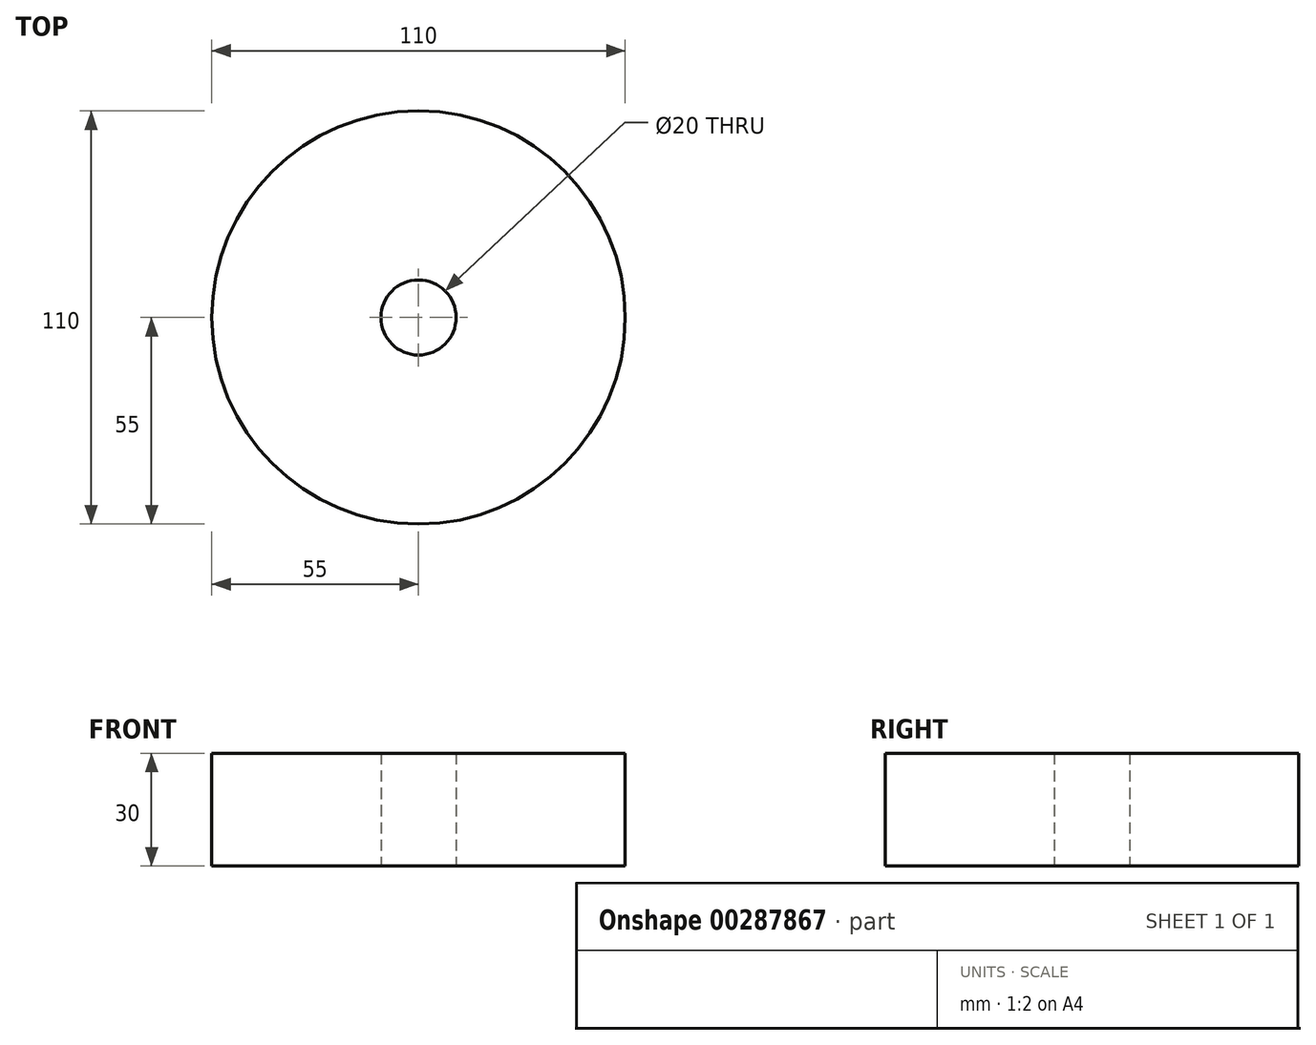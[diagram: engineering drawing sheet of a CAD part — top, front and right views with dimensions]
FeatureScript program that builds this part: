
annotation { "Feature Type Name" : "Feature", "Feature Type Description" : "" }
export const myFeature = defineFeature(function(context is Context, id is Id, definition is map)
    precondition{}
    {
        {
            var Q0;
            Q0=qCreatedBy(makeId("Top.planeOp"),FACE);
            var sketch = newSketch(context, id + "F0", { "sketchPlane" : qUnion([Q0])});
            skCircle(sketch, "E0", {"center": v(0, 0) * mm, "radius": 10 * mm});
            skCircle(sketch, "E1", {"center": v(0, 0) * mm, "radius": 55 * mm});
            skSolve(sketch);
        }
        {
            var Q0;
            Q0=makeQuery(id+"F0.imprint","IMPRINT",FACE,{"disambiguationData":[TD([[makeQuery(id+"F0.imprint","IMPRINT",EDGE,{"derivedFrom":sQuery(id+"F0.wireOp",EDGE,"E0")}),-1.0]])]});
            extrude(context, id + "F1", {"entities" : qUnion([Q0]), "depth" : 30 * mm});
        }
    });
